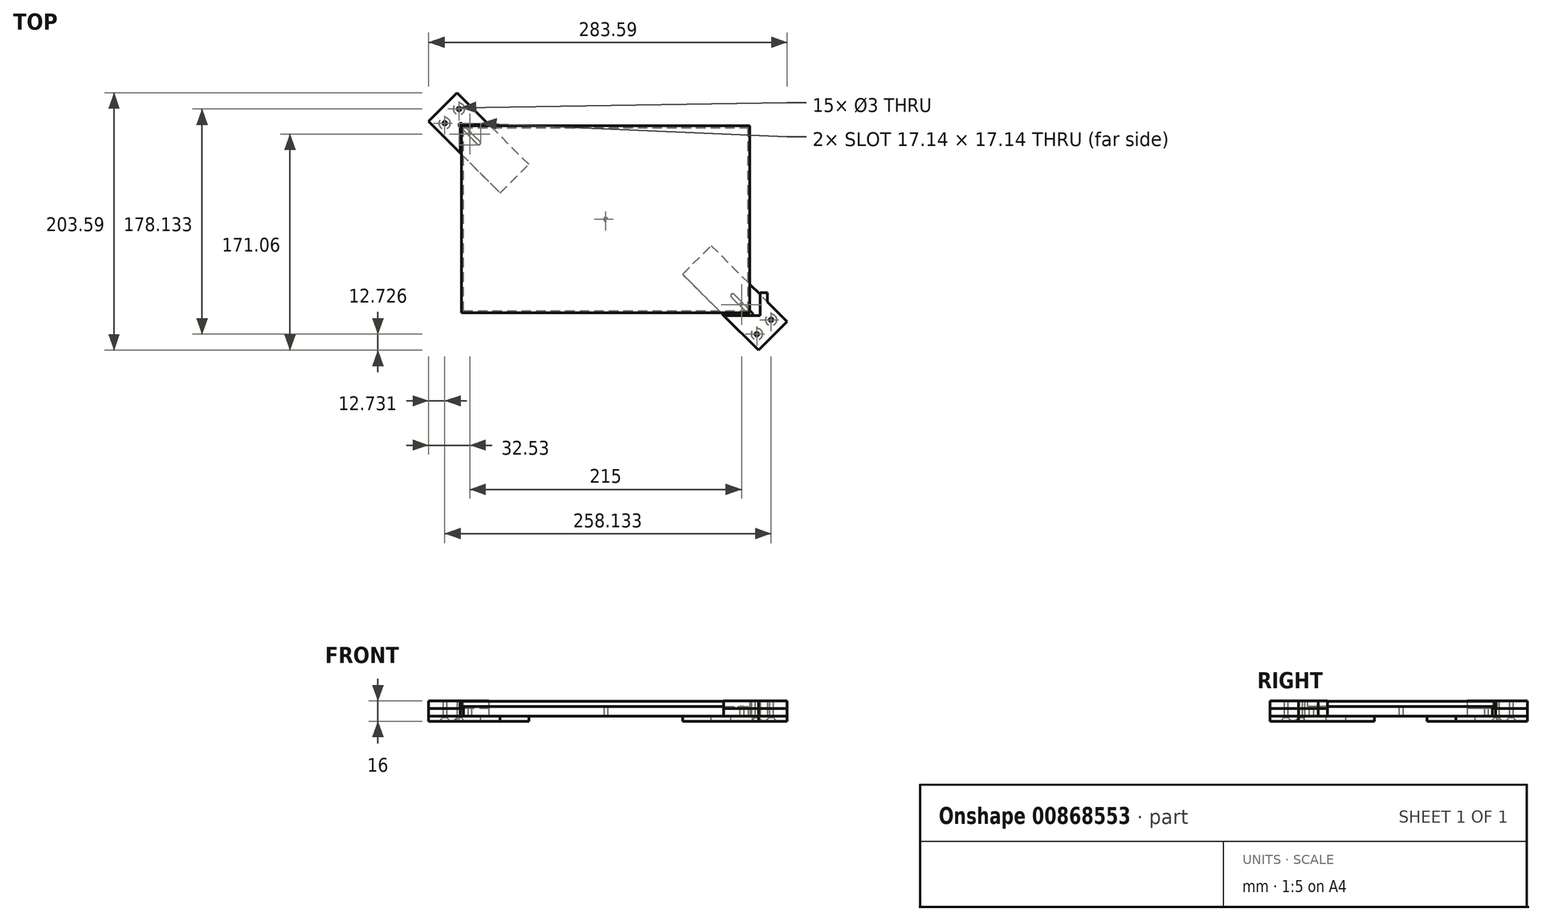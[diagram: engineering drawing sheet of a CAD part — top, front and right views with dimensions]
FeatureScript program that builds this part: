
annotation { "Feature Type Name" : "Feature", "Feature Type Description" : "" }
export const myFeature = defineFeature(function(context is Context, id is Id, definition is map)
    precondition{}
    {
        {
            assignVariable(context, id + "F0", {"name" : "printPlateThickness", "anyValue" : 7.67 * mm});
        }
        {
            var Q0;
            Q0=qCreatedBy(makeId("Top.planeOp"),FACE);
            var sketch = newSketch(context, id + "F1", { "sketchPlane" : qUnion([Q0])});
            skLineSegment(sketch, "E0.bottom", {"start": v(0, 0) * mm, "end": v(225, 0) * mm});
            skLineSegment(sketch, "E0.top", {"start": v(0, 145) * mm, "end": v(225, 145) * mm});
            skLineSegment(sketch, "E0.left", {"start": v(0, 0) * mm, "end": v(0, 145) * mm});
            skLineSegment(sketch, "E0.right", {"start": v(225, 0) * mm, "end": v(225, 145) * mm});
            skCircle(sketch, "E1", {"center": v(5, 140) * mm, "radius": 1.5 * mm});
            skCircle(sketch, "E2", {"center": v(220, 5) * mm, "radius": 1.5 * mm});
            skLineSegment(sketch, "E3.bottom", {"start": v(-1.5, 146.5) * mm, "end": v(226.5, 146.5) * mm});
            skLineSegment(sketch, "E3.top", {"start": v(-1.5, -1.5) * mm, "end": v(226.5, -1.5) * mm});
            skLineSegment(sketch, "E3.left", {"start": v(-1.5, 146.5) * mm, "end": v(-1.5, -1.5) * mm});
            skLineSegment(sketch, "E3.right", {"start": v(226.5, 146.5) * mm, "end": v(226.5, -1.5) * mm});
            skLineSegment(sketch, "E4", {"start": v(0, 0) * mm, "end": v(225, 145) * mm, "construction": true});
            skLineSegment(sketch, "E5", {"start": v(0, 145) * mm, "end": v(225, 0) * mm, "construction": true});
            skCircle(sketch, "E6", {"center": v(112.5, 72.5) * mm, "radius": 1.5 * mm});
            skSolve(sketch);
        }
        {
            var Q0;
            Q0=makeQuery(id+"F1.imprint","IMPRINT",FACE,{"disambiguationData":[TD([[makeQuery(id+"F1.imprint","IMPRINT",EDGE,{"derivedFrom":sQuery(id+"F1.wireOp",EDGE,"E0.bottom")}),1.0]])]});
            extrude(context, id + "F2", {"entities" : qUnion([Q0]), "depth" : getVariable(context, 'printPlateThickness'), "offsetDistance" : 25 * mm});
        }
        {
            var Q0;
            Q0=makeQuery(id+"F1.imprint","IMPRINT",FACE,{"disambiguationData":[TD([[makeQuery(id+"F1.imprint","IMPRINT",EDGE,{"derivedFrom":sQuery(id+"F1.wireOp",EDGE,"E0.bottom")}),1.0]])]});
            var Q1;
            Q1=makeQuery(id+"F1.imprint","IMPRINT",FACE,{"disambiguationData":[TD([[makeQuery(id+"F1.imprint","IMPRINT",EDGE,{"derivedFrom":sQuery(id+"F1.wireOp",EDGE,"E0.bottom")}),-1.0]])]});
            var Q2;
            Q2=makeQuery(id+"F1.imprint","IMPRINT",FACE,{"disambiguationData":[TD([[makeQuery(id+"F1.imprint","IMPRINT",EDGE,{"derivedFrom":sQuery(id+"F1.wireOp",EDGE,"E1")}),1.0]])]});
            var Q3;
            Q3=makeQuery(id+"F1.imprint","IMPRINT",FACE,{"disambiguationData":[TD([[makeQuery(id+"F1.imprint","IMPRINT",EDGE,{"derivedFrom":sQuery(id+"F1.wireOp",EDGE,"E2")}),1.0]])]});
            var Q4;
            Q4=makeQuery(id+"F1.imprint","IMPRINT",FACE,{"disambiguationData":[TD([[makeQuery(id+"F1.imprint","IMPRINT",EDGE,{"derivedFrom":sQuery(id+"F1.wireOp",EDGE,"E6")}),1.0]])]});
            extrude(context, id + "F3", {"entities" : qUnion([Q0, Q1, Q2, Q3, Q4]), "depth" : 4 * mm + getVariable(context, 'printPlateThickness'), "offsetDistance" : 25 * mm, "hasSecondDirection" : true, "secondDirectionOppositeDirection" : false, "secondDirectionDepth" : getVariable(context, 'printPlateThickness')});
        }
        {
            var Q0;
            Q0=makeQuery(id+"F2.opExtrude","CAP_FACE",FACE,{"disambiguationData":[OSD([sQuery(id+"F1.wireOp",EDGE,"E0.bottom"),sQuery(id+"F1.wireOp",EDGE,"E0.top"),sQuery(id+"F1.wireOp",EDGE,"E0.left"),sQuery(id+"F1.wireOp",EDGE,"E0.right"),sQuery(id+"F1.wireOp",EDGE,"E1"),sQuery(id+"F1.wireOp",EDGE,"E2"),sQuery(id+"F1.wireOp",EDGE,"E6")])],"isStart":true});
            var sketch = newSketch(context, id + "F4", { "sketchPlane" : qUnion([Q0])});
            skLineSegment(sketch, "E7", {"start": v(195.96, -51.67) * mm, "end": v(256.06, 8.44) * mm});
            skLineSegment(sketch, "E8", {"start": v(256.06, 8.44) * mm, "end": v(233.44, 31.06) * mm});
            skLineSegment(sketch, "E9", {"start": v(233.44, 31.06) * mm, "end": v(173.33, -29.04) * mm});
            skLineSegment(sketch, "E10", {"start": v(173.33, -29.04) * mm, "end": v(195.96, -51.67) * mm});
            skLineSegment(sketch, "E11", {"start": v(29.04, -93.33) * mm, "end": v(51.67, -115.96) * mm});
            skLineSegment(sketch, "E12", {"start": v(51.67, -115.96) * mm, "end": v(-4.9, -172.53) * mm});
            skLineSegment(sketch, "E13", {"start": v(-4.9, -172.53) * mm, "end": v(-27.53, -149.9) * mm});
            skLineSegment(sketch, "E14", {"start": v(-27.53, -149.9) * mm, "end": v(29.04, -93.33) * mm});
            skLineSegment(sketch, "E15", {"start": v(178.75, -46.25) * mm, "end": v(265.94, 40.94) * mm, "construction": true});
            skLineSegment(sketch, "E16", {"start": v(-26.7, -171.7) * mm, "end": v(38.94, -106.06) * mm, "construction": true});
            skPoint(sketch, "E17", {"position": v(184.64, -40.36) * mm});
            skPoint(sketch, "E18", {"position": v(40.36, -104.64) * mm});
            skPoint(sketch, "E19", {"position": v(243.33, 7.02) * mm});
            skPoint(sketch, "E20", {"position": v(232.02, 18.33) * mm});
            skPoint(sketch, "E21", {"position": v(-3.49, -159.8) * mm});
            skPoint(sketch, "E22", {"position": v(-14.8, -148.49) * mm});
            skPoint(sketch, "E23", {"position": v(227.07, 2.07) * mm});
            skPoint(sketch, "E24", {"position": v(212.93, -12.07) * mm});
            skPoint(sketch, "E25", {"position": v(-2.07, -147.07) * mm});
            skPoint(sketch, "E26", {"position": v(12.07, -132.93) * mm});
            skCircle(sketch, "E27", {"center": v(232.02, 18.33) * mm, "radius": 1.5 * mm});
            skCircle(sketch, "E28", {"center": v(243.33, 7.02) * mm, "radius": 1.5 * mm});
            skCircle(sketch, "E29", {"center": v(-3.49, -159.8) * mm, "radius": 1.5 * mm});
            skCircle(sketch, "E30", {"center": v(-14.8, -148.49) * mm, "radius": 1.5 * mm});
            skCircle(sketch, "E31", {"center": v(-2.07, -147.07) * mm, "radius": 1.5 * mm});
            skCircle(sketch, "E32", {"center": v(12.07, -132.93) * mm, "radius": 1.5 * mm});
            skCircle(sketch, "E33", {"center": v(212.93, -12.07) * mm, "radius": 1.5 * mm});
            skCircle(sketch, "E34", {"center": v(227.07, 2.07) * mm, "radius": 1.5 * mm});
            skLineSegment(sketch, "E35", {"start": v(-4.75, -144.4) * mm, "end": v(0.98, -150.12) * mm, "construction": true});
            skLineSegment(sketch, "E36", {"start": v(9.51, -130.37) * mm, "end": v(14.75, -135.61) * mm, "construction": true});
            skLineSegment(sketch, "E37", {"start": v(209.9, -9.03) * mm, "end": v(216.8, -15.95) * mm, "construction": true});
            skLineSegment(sketch, "E38", {"start": v(223.66, 5.48) * mm, "end": v(232.75, -3.61) * mm, "construction": true});
            skLineSegment(sketch, "E39", {"start": v(-1.01, -148.13) * mm, "end": v(13.13, -133.99) * mm});
            skLineSegment(sketch, "E40", {"start": v(-3.13, -146.01) * mm, "end": v(11.01, -131.87) * mm});
            skLineSegment(sketch, "E41", {"start": v(213.99, -13.13) * mm, "end": v(228.13, 1.01) * mm});
            skLineSegment(sketch, "E42", {"start": v(226.01, 3.13) * mm, "end": v(211.87, -11.01) * mm});
            skSolve(sketch);
        }
        {
            var Q0;
            {var subQ6=sQuery(id+"F4.wireOp",EDGE,"E11");Q0=makeQuery(id+"F4.imprint","IMPRINT",FACE,{"disambiguationData":[TD([[makeQuery(id+"F4.imprint","IMPRINT",EDGE,{"derivedFrom":subQ6}),-1.0]])]});}
            var Q1;
            {var subQ1=sQuery(id+"F4.wireOp",EDGE,"E13");Q1=makeQuery(id+"F4.imprint","IMPRINT",FACE,{"disambiguationData":[TD([[makeQuery(id+"F4.imprint","IMPRINT",EDGE,{"derivedFrom":subQ1}),-1.0]])]});}
            extrude(context, id + "F5", {"entities" : qUnion([Q0, Q1]), "depth" : 4 * mm, "offsetDistance" : 25 * mm});
        }
        {
            var Q0;
            {var subQ1=sQuery(id+"F4.wireOp",EDGE,"E8");Q0=makeQuery(id+"F4.imprint","IMPRINT",FACE,{"disambiguationData":[TD([[makeQuery(id+"F4.imprint","IMPRINT",EDGE,{"derivedFrom":subQ1}),1.0]])]});}
            var Q1;
            {var subQ0=sQuery(id+"F4.wireOp",EDGE,"E10");Q1=makeQuery(id+"F4.imprint","IMPRINT",FACE,{"disambiguationData":[TD([[makeQuery(id+"F4.imprint","IMPRINT",EDGE,{"derivedFrom":subQ0}),1.0]])]});}
            extrude(context, id + "F6", {"entities" : qUnion([Q0, Q1]), "depth" : 4 * mm, "offsetDistance" : 25 * mm});
        }
        {
            var Q0;
            Q0=makeQuery(id+"F6.opExtrude","CAP_EDGE",EDGE,{"disambiguationData":[OSD([sQuery(id+"F4.wireOp",EDGE,"E27")])],"isStart":false});
            var Q1;
            Q1=makeQuery(id+"F6.opExtrude","CAP_EDGE",EDGE,{"disambiguationData":[OSD([sQuery(id+"F4.wireOp",EDGE,"E28")])],"isStart":false});
            var Q2;
            Q2=makeQuery(id+"F5.opExtrude","CAP_EDGE",EDGE,{"disambiguationData":[OSD([sQuery(id+"F4.wireOp",EDGE,"E30")])],"isStart":false});
            var Q3;
            Q3=makeQuery(id+"F5.opExtrude","CAP_EDGE",EDGE,{"disambiguationData":[OSD([sQuery(id+"F4.wireOp",EDGE,"E29")])],"isStart":false});
            chamfer(context, id + "F7", {"entities" : qUnion([Q0, Q1, Q2, Q3]), "width" : 3 * mm, "tangentPropagation" : true});
        }
        {
            var Q0;
            Q0=makeQuery(id+"F5.opExtrude","CAP_FACE",FACE,{"disambiguationData":[OSD([sQuery(id+"F4.wireOp",EDGE,"E11"),sQuery(id+"F4.wireOp",EDGE,"E12"),sQuery(id+"F4.wireOp",EDGE,"E13"),sQuery(id+"F4.wireOp",EDGE,"E14"),sQuery(id+"F4.wireOp",EDGE,"E29"),sQuery(id+"F4.wireOp",EDGE,"E30"),sQuery(id+"F4.wireOp",EDGE,"E31"),sQuery(id+"F4.wireOp",EDGE,"E32"),sQuery(id+"F4.wireOp",EDGE,"E39"),sQuery(id+"F4.wireOp",EDGE,"E40")])],"isStart":true});
            var sketch = newSketch(context, id + "F8", { "sketchPlane" : qUnion([Q0])});
            skLineSegment(sketch, "E43", {"start": v(-4.9, 172.53) * mm, "end": v(20.13, 147.5) * mm});
            skLineSegment(sketch, "E44", {"start": v(20.13, 147.5) * mm, "end": v(-2.5, 147.5) * mm});
            skLineSegment(sketch, "E45", {"start": v(-2.5, 147.5) * mm, "end": v(-2.5, 124.87) * mm});
            skLineSegment(sketch, "E46", {"start": v(-2.5, 124.87) * mm, "end": v(-27.53, 149.9) * mm});
            skLineSegment(sketch, "E47", {"start": v(-27.53, 149.9) * mm, "end": v(-4.9, 172.53) * mm});
            skLineSegment(sketch, "E48", {"start": v(-16.21, 161.21) * mm, "end": v(27.94, 117.06) * mm, "construction": true});
            skCircle(sketch, "E49", {"center": v(-3.49, 159.8) * mm, "radius": 1.5 * mm});
            skCircle(sketch, "E50", {"center": v(-14.8, 148.49) * mm, "radius": 1.5 * mm});
            skSolve(sketch);
        }
        {
            var Q0;
            Q0=qSketchRegion(id+"F8",true);
            extrude(context, id + "F9", {"entities" : qUnion([Q0]), "depth" : 6 * mm, "offsetDistance" : 25 * mm});
        }
        {
            var Q0;
            {var subQ5=sQuery(id+"F8.wireOp",EDGE,"E43");Q0=makeQuery(id+"F8.imprint","IMPRINT",FACE,{"disambiguationData":[TD([[makeQuery(id+"F8.imprint","IMPRINT",EDGE,{"derivedFrom":subQ5}),1.0]])]});}
            extrude(context, id + "F10", {"entities" : qUnion([Q0]), "depth" : 12 * mm, "offsetDistance" : 25 * mm, "hasSecondDirection" : true, "secondDirectionOppositeDirection" : false, "secondDirectionDepth" : 6 * mm});
        }
        {
            var Q0;
            {var subQ1=sQuery(id+"F4.wireOp",EDGE,"E8");Q0=makeQuery(id+"F4.imprint","IMPRINT",FACE,{"disambiguationData":[TD([[makeQuery(id+"F4.imprint","IMPRINT",EDGE,{"derivedFrom":subQ1}),1.0]])]});}
            var sketch = newSketch(context, id + "F11", { "sketchPlane" : qUnion([Q0])});
            skLineSegment(sketch, "E51", {"start": v(205.87, 3.5) * mm, "end": v(234.5, 3.5) * mm});
            skLineSegment(sketch, "E52", {"start": v(234.5, 3.5) * mm, "end": v(234.5, -14.5) * mm});
            skLineSegment(sketch, "E53", {"start": v(234.5, -14.5) * mm, "end": v(240.5, -14.5) * mm});
            skLineSegment(sketch, "E54", {"start": v(240.5, -14.5) * mm, "end": v(240.5, -7.13) * mm});
            skLineSegment(sketch, "E55", {"start": v(240.5, -7.13) * mm, "end": v(256.06, 8.44) * mm});
            skLineSegment(sketch, "E56", {"start": v(256.06, 8.44) * mm, "end": v(233.44, 31.06) * mm});
            skLineSegment(sketch, "E57", {"start": v(233.44, 31.06) * mm, "end": v(205.87, 3.5) * mm});
            skSolve(sketch);
        }
        {
            var Q0;
            {var subQ7=sQuery(id+"F11.wireOp",EDGE,"E55");Q0=makeQuery(id+"F11.imprint","IMPRINT",FACE,{"disambiguationData":[TD([[makeQuery(id+"F11.imprint","IMPRINT",EDGE,{"derivedFrom":subQ7}),1.0]])]});}
            var Q1;
            {var subQ0=sQuery(id+"F11.wireOp",EDGE,"E53");Q1=makeQuery(id+"F11.imprint","IMPRINT",FACE,{"disambiguationData":[TD([[makeQuery(id+"F11.imprint","IMPRINT",EDGE,{"derivedFrom":subQ0}),1.0]])]});}
            extrude(context, id + "F12", {"entities" : qUnion([Q0, Q1]), "oppositeDirection" : true, "depth" : 6 * mm, "offsetDistance" : 25 * mm});
        }
        {
            var Q0;
            {var subQ7=sQuery(id+"F11.wireOp",EDGE,"E55");Q0=makeQuery(id+"F11.imprint","IMPRINT",FACE,{"disambiguationData":[TD([[makeQuery(id+"F11.imprint","IMPRINT",EDGE,{"derivedFrom":subQ7}),1.0]])]});}
            var Q1;
            {var subQ0=sQuery(id+"F11.wireOp",EDGE,"E53");Q1=makeQuery(id+"F11.imprint","IMPRINT",FACE,{"disambiguationData":[TD([[makeQuery(id+"F11.imprint","IMPRINT",EDGE,{"derivedFrom":subQ0}),1.0]])]});}
            extrude(context, id + "F13", {"entities" : qUnion([Q0, Q1]), "oppositeDirection" : true, "depth" : 12 * mm, "offsetDistance" : 25 * mm, "hasSecondDirection" : true, "secondDirectionOppositeDirection" : true, "secondDirectionDepth" : 6 * mm});
        }
    });
